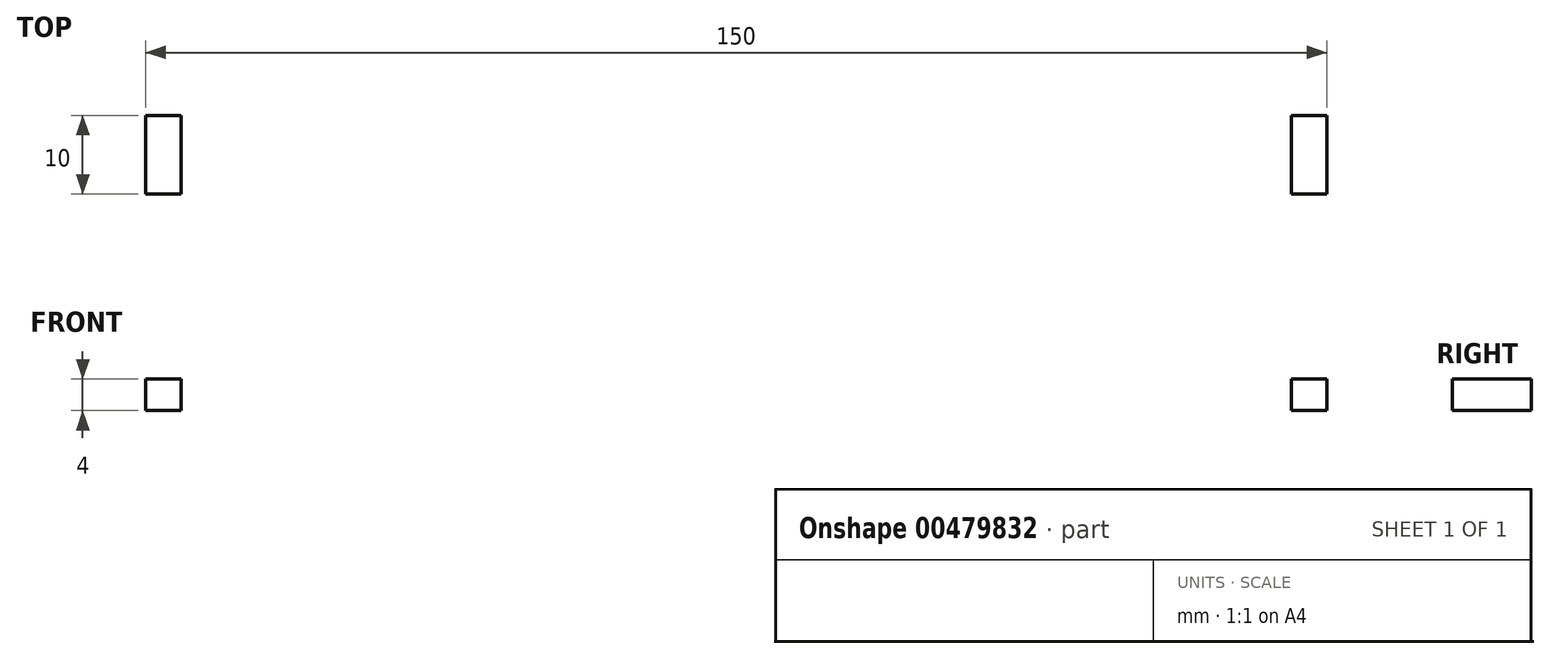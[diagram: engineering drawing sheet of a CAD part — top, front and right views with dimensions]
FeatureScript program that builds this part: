
annotation { "Feature Type Name" : "Feature", "Feature Type Description" : "" }
export const myFeature = defineFeature(function(context is Context, id is Id, definition is map)
    precondition{}
    {
        {
            var Q0;
            Q0=qCreatedBy(makeId("Top.planeOp"),FACE);
            var sketch = newSketch(context, id + "F0", { "sketchPlane" : qUnion([Q0])});
            skLineSegment(sketch, "E0.bottom", {"start": v(0, 0) * mm, "end": v(150, 0) * mm});
            skLineSegment(sketch, "E0.top", {"start": v(0, 56) * mm, "end": v(150, 56) * mm});
            skLineSegment(sketch, "E0.left", {"start": v(0, 0) * mm, "end": v(0, 56) * mm});
            skLineSegment(sketch, "E0.right", {"start": v(150, 0) * mm, "end": v(150, 56) * mm});
            skPoint(sketch, "E1.top.end.orphan", {"position": v(145.5, 10) * mm});
            skPoint(sketch, "E2.top.end.orphan", {"position": v(4.5, 10) * mm});
            skLineSegment(sketch, "E3.bottom", {"start": v(0, 0) * mm, "end": v(4.5, 0) * mm});
            skLineSegment(sketch, "E3.top", {"start": v(0, 10) * mm, "end": v(4.5, 10) * mm});
            skLineSegment(sketch, "E3.left", {"start": v(0, 0) * mm, "end": v(0, 10) * mm});
            skLineSegment(sketch, "E3.right", {"start": v(4.5, 0) * mm, "end": v(4.5, 10) * mm});
            skLineSegment(sketch, "E4.bottom", {"start": v(150, 0) * mm, "end": v(145.5, 0) * mm});
            skLineSegment(sketch, "E4.top", {"start": v(150, 10) * mm, "end": v(145.5, 10) * mm});
            skLineSegment(sketch, "E4.left", {"start": v(150, 0) * mm, "end": v(150, 10) * mm});
            skLineSegment(sketch, "E4.right", {"start": v(145.5, 0) * mm, "end": v(145.5, 10) * mm});
            skSolve(sketch);
        }
        {
            var Q0;
            Q0=makeQuery(id+"F0.imprint","IMPRINT",FACE,{"disambiguationData":[TD([[makeQuery(id+"F0.imprint","IMPRINT",EDGE,{"derivedFrom":sQuery(id+"F0.wireOp",EDGE,"E0.bottom")}),1.0]])]});
            extrude(context, id + "F1", {"entities" : qUnion([Q0]), "depth" : 4 * mm});
        }
    });
